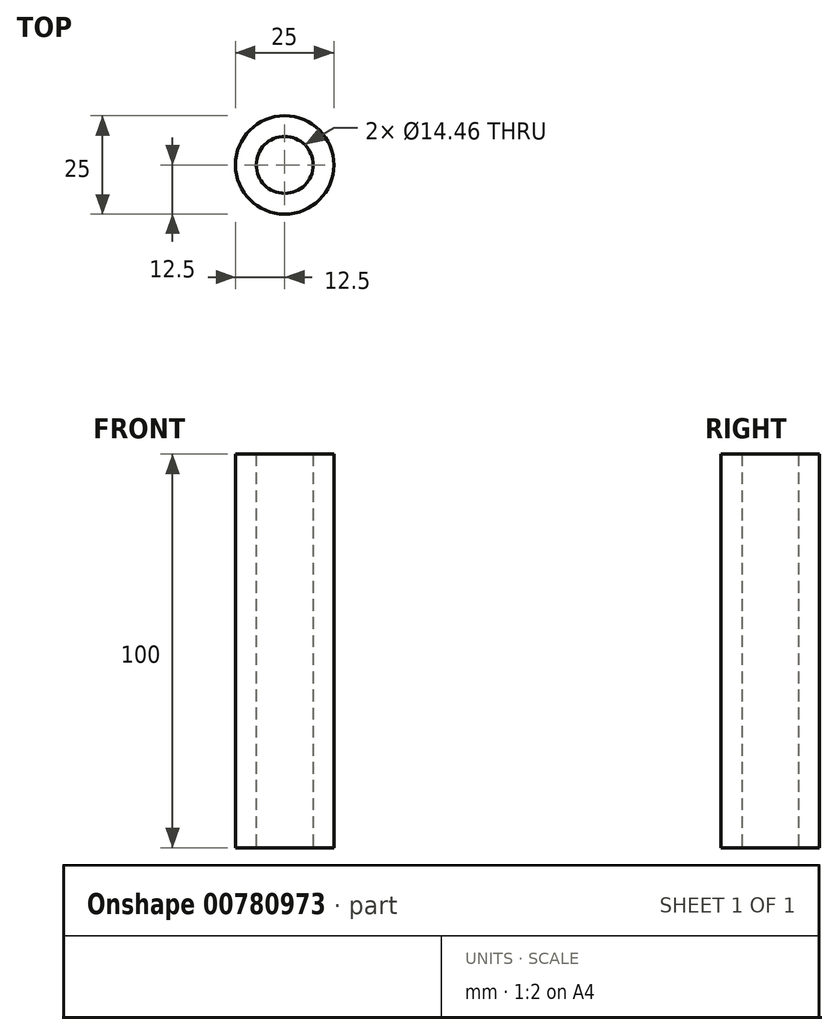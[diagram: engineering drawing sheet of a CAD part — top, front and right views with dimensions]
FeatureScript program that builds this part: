
annotation { "Feature Type Name" : "Feature", "Feature Type Description" : "" }
export const myFeature = defineFeature(function(context is Context, id is Id, definition is map)
    precondition{}
    {
        {
            var Q0;
            Q0=qCreatedBy(makeId("Top.planeOp"),FACE);
            var sketch = newSketch(context, id + "F0", { "sketchPlane" : qUnion([Q0])});
            skCircle(sketch, "E0", {"center": v(0, 0) * mm, "radius": 12.5 * mm});
            skCircle(sketch, "E1", {"center": v(0, 0) * mm, "radius": 7.23 * mm});
            skSolve(sketch);
        }
        {
            var Q0;
            Q0=makeQuery(id+"F0.imprint","IMPRINT",FACE,{"disambiguationData":[TD([[makeQuery(id+"F0.imprint","IMPRINT",EDGE,{"derivedFrom":sQuery(id+"F0.wireOp",EDGE,"E0")}),1.0]])]});
            extrude(context, id + "F1", {"entities" : qUnion([Q0]), "depth" : 100 * mm, "offsetDistance" : 25.4 * mm});
        }
    });
